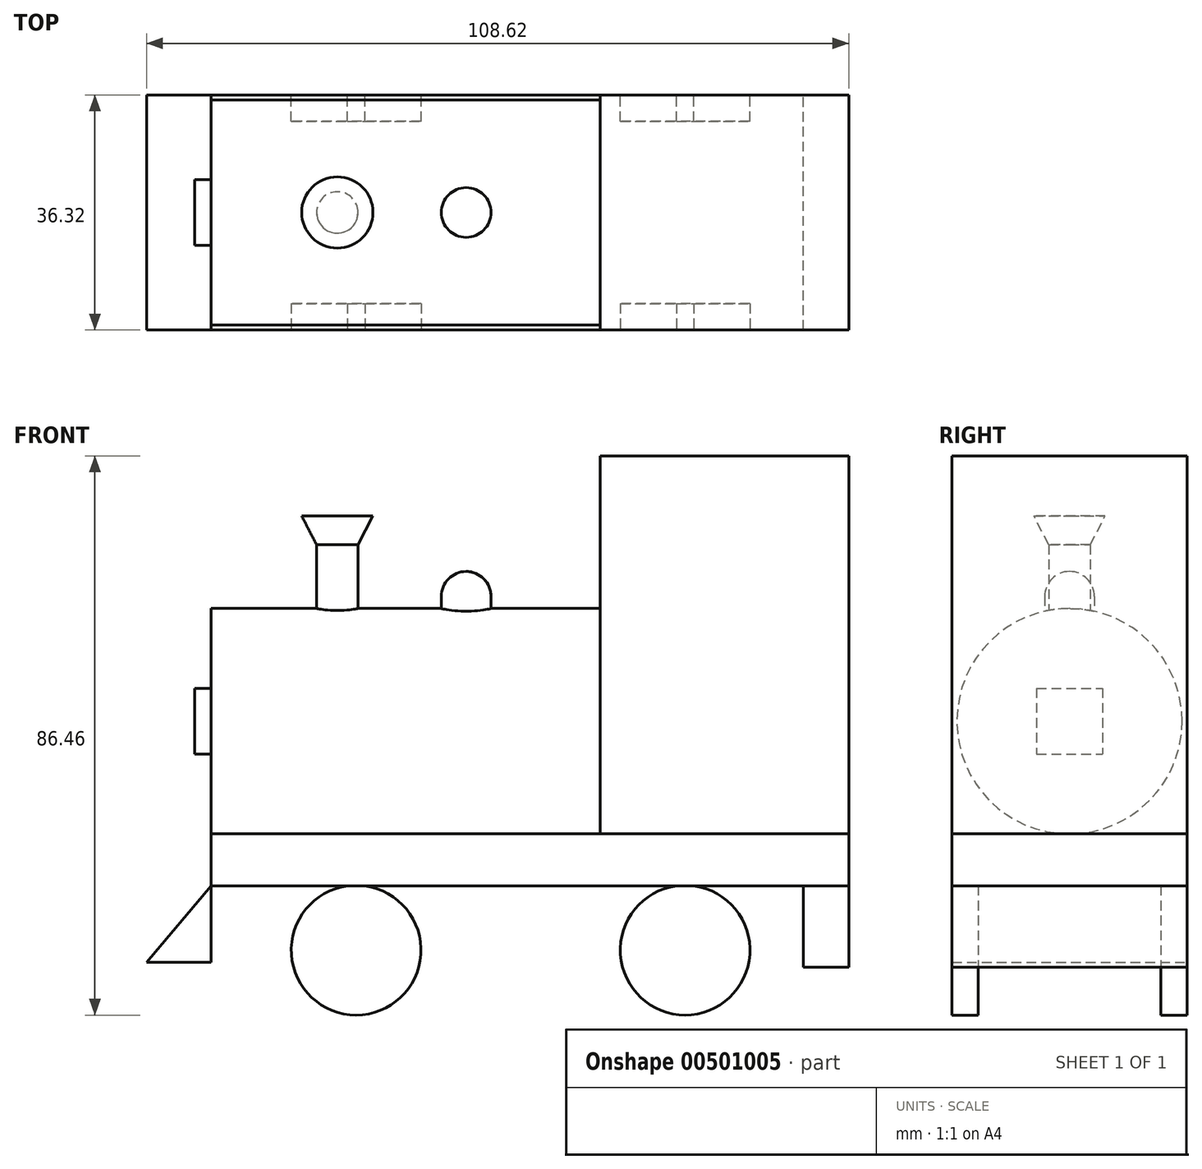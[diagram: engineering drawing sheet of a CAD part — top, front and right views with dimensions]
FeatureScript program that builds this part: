
annotation { "Feature Type Name" : "Feature", "Feature Type Description" : "" }
export const myFeature = defineFeature(function(context is Context, id is Id, definition is map)
    precondition{}
    {
        {
            var Q0;
            Q0=qCreatedBy(makeId("Front.planeOp"),FACE);
            var sketch = newSketch(context, id + "F0", { "sketchPlane" : qUnion([Q0])});
            skLineSegment(sketch, "E0.bottom", {"start": v(-47.1, -11.4) * mm, "end": v(51.53, -11.4) * mm});
            skLineSegment(sketch, "E0.top", {"start": v(-47.1, -19.43) * mm, "end": v(51.53, -19.43) * mm});
            skLineSegment(sketch, "E0.left", {"start": v(-47.1, -11.4) * mm, "end": v(-47.1, -19.43) * mm});
            skLineSegment(sketch, "E0.right", {"start": v(51.53, -11.4) * mm, "end": v(51.53, -19.43) * mm});
            skSolve(sketch);
        }
        {
            var Q0;
            Q0 = qSketchRegion(id + "F0", true);
            extrude(context, id + "F1", {"entities" : qUnion([Q0]), "oppositeDirection" : true, "depth" : 36.32 * mm, "symmetric" : true});
        }
        {
            var Q0;
            Q0=makeQuery(id+"F1.opExtrude","SWEPT_FACE",FACE,{"disambiguationData":[OSD([sQuery(id+"F0.wireOp",EDGE,"E0.left")])]});
            var sketch = newSketch(context, id + "F2", { "sketchPlane" : qUnion([Q0])});
            skCircle(sketch, "E1", {"center": v(0, 6.03) * mm, "radius": 17.42 * mm});
            skSolve(sketch);
        }
        {
            var Q0;
            Q0 = qSketchRegion(id + "F2", true);
            extrude(context, id + "F3", {"entities" : qUnion([Q0]), "operationType" : NewBodyOperationType.ADD, "oppositeDirection" : true, "depth" : 60.2 * mm});
        }
        {
            var Q0;
            Q0=makeQuery(id+"F3.opExtrude","CAP_FACE",FACE,{"disambiguationData":[OSD([sQuery(id+"F2.wireOp",EDGE,"E1")])],"isStart":false});
            var sketch = newSketch(context, id + "F4", { "sketchPlane" : qUnion([Q0])});
            skLineSegment(sketch, "E2.0", {"start": v(18.16, -11.4) * mm, "end": v(-18.16, -11.4) * mm});
            skLineSegment(sketch, "E3.top", {"start": v(18.16, 47.04) * mm, "end": v(-18.16, 47.04) * mm});
            skLineSegment(sketch, "E3.left", {"start": v(18.16, -11.4) * mm, "end": v(18.16, 47.04) * mm});
            skLineSegment(sketch, "E3.right", {"start": v(-18.16, -11.4) * mm, "end": v(-18.16, 47.04) * mm});
            skPoint(sketch, "E3.middle", {"position": v(0, 17.82) * mm});
            skPoint(sketch, "E3.middle.positionSnap0", {"position": v(0, -11.4) * mm});
            skPoint(sketch, "E3.centerSnap0", {"position": v(0, -11.4) * mm});
            skSolve(sketch);
        }
        {
            var Q0;
            Q0 = qSketchRegion(id + "F4", true);
            var Q1;
            Q1=makeQuery(id+"F1.opExtrude","SWEPT_FACE",FACE,{"disambiguationData":[OSD([sQuery(id+"F0.wireOp",EDGE,"E0.right")])]});
            extrude(context, id + "F5", {"entities" : qUnion([Q0]), "endBound" : BoundingType.UP_TO_SURFACE, "endBoundEntityFace" : qUnion([Q1]), "depth" : 17.78 * mm});
        }
        {
            var Q0;
            Q0=qCreatedBy(makeId("Front.planeOp"),FACE);
            var sketch = newSketch(context, id + "F6", { "sketchPlane" : qUnion([Q0])});
            skLineSegment(sketch, "E4", {"start": v(-27.6, 18.2) * mm, "end": v(-24.39, 18.2) * mm});
            skLineSegment(sketch, "E5", {"start": v(-24.39, 18.2) * mm, "end": v(-24.39, 33.31) * mm});
            skLineSegment(sketch, "E6", {"start": v(-24.39, 33.31) * mm, "end": v(-22.08, 37.76) * mm});
            skLineSegment(sketch, "E7", {"start": v(-27.6, 18.2) * mm, "end": v(-27.6, 48.43) * mm, "construction": true});
            skLineSegment(sketch, "E8", {"start": v(-22.08, 37.76) * mm, "end": v(-27.6, 37.76) * mm});
            skLineSegment(sketch, "E9", {"start": v(-27.6, 37.76) * mm, "end": v(-27.6, 18.2) * mm});
            skSolve(sketch);
        }
        {
            var Q0;
            Q0 = qSketchRegion(id + "F6", true);
            var Q1;
            Q1=sQuery(id+"F6.wireOp",EDGE,"E7");
            revolve(context, id + "F7", {"operationType" : NewBodyOperationType.ADD, "surfaceOperationType" : NewSurfaceOperationType.NEW, "entities" : qUnion([Q0]), "axis" : qUnion([Q1]), "revolveType" : RevolveType.FULL});
        }
        {
            var Q0;
            Q0=makeQuery(id+"F1.opExtrude","CAP_FACE",FACE,{"disambiguationData":[OSD([sQuery(id+"F0.wireOp",EDGE,"E0.bottom"),sQuery(id+"F0.wireOp",EDGE,"E0.top"),sQuery(id+"F0.wireOp",EDGE,"E0.left"),sQuery(id+"F0.wireOp",EDGE,"E0.right")])],"isStart":false});
            var sketch = newSketch(context, id + "F8", { "sketchPlane" : qUnion([Q0])});
            skCircle(sketch, "E10", {"center": v(24.68, -29.38) * mm, "radius": 10.04 * mm});
            skCircle(sketch, "E11", {"center": v(-26.22, -29.38) * mm, "radius": 10.04 * mm});
            skSolve(sketch);
        }
        {
            var Q0;
            Q0 = qSketchRegion(id + "F8", true);
            extrude(context, id + "F9", {"entities" : qUnion([Q0]), "operationType" : NewBodyOperationType.ADD, "oppositeDirection" : true, "depth" : 4.06 * mm});
        }
        {
            var Q0;
            Q0=makeQuery(id+"F1.opExtrude","SWEPT_BODY",BODY,{"disambiguationData":[OSD([sQuery(id+"F0.wireOp",EDGE,"E0.bottom"),sQuery(id+"F0.wireOp",EDGE,"E0.top"),sQuery(id+"F0.wireOp",EDGE,"E0.left"),sQuery(id+"F0.wireOp",EDGE,"E0.right")])]});
            var Q1;
            Q1=qCreatedBy(makeId("Front.planeOp"),FACE);
            mirror(context, id + "F10", {"entities" : qUnion([Q0]), "mirrorPlane" : qUnion([Q1])});
        }
        {
            var Q0;
            Q0=makeQuery(id+"F10.opPattern","COPY",FACE,{"derivedFrom":makeQuery(id+"F1.opExtrude","CAP_FACE",FACE,{"disambiguationData":[OSD([sQuery(id+"F0.wireOp",EDGE,"E0.bottom"),sQuery(id+"F0.wireOp",EDGE,"E0.top"),sQuery(id+"F0.wireOp",EDGE,"E0.left"),sQuery(id+"F0.wireOp",EDGE,"E0.right")])],"isStart":true}),"instanceName":"1"});
            var sketch = newSketch(context, id + "F11", { "sketchPlane" : qUnion([Q0])});
            skLineSegment(sketch, "E12", {"start": v(47.1, -19.43) * mm, "end": v(57.1, -31.23) * mm});
            skLineSegment(sketch, "E13", {"start": v(57.1, -31.23) * mm, "end": v(47.1, -31.23) * mm});
            skLineSegment(sketch, "E14", {"start": v(47.1, -31.23) * mm, "end": v(47.1, -19.43) * mm});
            skSolve(sketch);
        }
        {
            var Q0;
            Q0 = qSketchRegion(id + "F11", true);
            var Q1;
            Q1=makeQuery(id+"F10.opPattern","COPY",FACE,{"derivedFrom":makeQuery(id+"F9.boolean.opBoolean","MERGE",FACE,{"derivedFrom":[makeQuery(id+"F1.opExtrude","CAP_FACE",FACE,{"disambiguationData":[OSD([sQuery(id+"F0.wireOp",EDGE,"E0.bottom"),sQuery(id+"F0.wireOp",EDGE,"E0.top"),sQuery(id+"F0.wireOp",EDGE,"E0.left"),sQuery(id+"F0.wireOp",EDGE,"E0.right")])],"isStart":false}),makeQuery(id+"F9.opExtrude","CAP_FACE",FACE,{"disambiguationData":[OSD([sQuery(id+"F8.wireOp",EDGE,"E10")])],"isStart":true}),makeQuery(id+"F9.opExtrude","CAP_FACE",FACE,{"disambiguationData":[OSD([sQuery(id+"F8.wireOp",EDGE,"E11")])],"isStart":true})]}),"instanceName":"1"});
            extrude(context, id + "F12", {"entities" : qUnion([Q0]), "endBound" : BoundingType.UP_TO_SURFACE, "oppositeDirection" : true, "endBoundEntityFace" : qUnion([Q1]), "depth" : 25.4 * mm});
        }
        {
            var Q0;
            Q0=qCreatedBy(makeId("Front.planeOp"),FACE);
            var sketch = newSketch(context, id + "F13", { "sketchPlane" : qUnion([Q0])});
            skLineSegment(sketch, "E15", {"start": v(-7.66, 17.2) * mm, "end": v(-3.81, 17.2) * mm});
            skLineSegment(sketch, "E16", {"start": v(-3.81, 17.2) * mm, "end": v(-3.81, 25.33) * mm});
            skLineSegment(sketch, "E17", {"start": v(-7.66, 17.2) * mm, "end": v(-7.66, 42.78) * mm, "construction": true});
            skArc(sketch, "E18", {"start": v(-3.81, 25.33) * mm, "mid": v(-4.94, 28.05) * mm, "end": v(-7.66, 29.18) * mm});
            skLineSegment(sketch, "E19", {"start": v(-7.66, 17.2) * mm, "end": v(-7.66, 29.18) * mm});
            skSolve(sketch);
        }
        {
            var Q0;
            Q0 = qSketchRegion(id + "F13", true);
            var Q1;
            Q1=sQuery(id+"F13.wireOp",EDGE,"E17");
            revolve(context, id + "F14", {"operationType" : NewBodyOperationType.ADD, "surfaceOperationType" : NewSurfaceOperationType.NEW, "entities" : qUnion([Q0]), "axis" : qUnion([Q1]), "revolveType" : RevolveType.FULL});
        }
        {
            var Q0;
            Q0=makeQuery(id+"F9.boolean.opBoolean","MERGE",FACE,{"derivedFrom":[makeQuery(id+"F1.opExtrude","CAP_FACE",FACE,{"disambiguationData":[OSD([sQuery(id+"F0.wireOp",EDGE,"E0.bottom"),sQuery(id+"F0.wireOp",EDGE,"E0.top"),sQuery(id+"F0.wireOp",EDGE,"E0.left"),sQuery(id+"F0.wireOp",EDGE,"E0.right")])],"isStart":false}),makeQuery(id+"F9.opExtrude","CAP_FACE",FACE,{"disambiguationData":[OSD([sQuery(id+"F8.wireOp",EDGE,"E10")])],"isStart":true}),makeQuery(id+"F9.opExtrude","CAP_FACE",FACE,{"disambiguationData":[OSD([sQuery(id+"F8.wireOp",EDGE,"E11")])],"isStart":true})]});
            var sketch = newSketch(context, id + "F15", { "sketchPlane" : qUnion([Q0])});
            skLineSegment(sketch, "E20.bottom", {"start": v(-51.53, -19.43) * mm, "end": v(-44.5, -19.43) * mm});
            skLineSegment(sketch, "E20.top", {"start": v(-51.53, -32.03) * mm, "end": v(-44.5, -32.03) * mm});
            skLineSegment(sketch, "E20.left", {"start": v(-51.53, -19.43) * mm, "end": v(-51.53, -32.03) * mm});
            skLineSegment(sketch, "E20.right", {"start": v(-44.5, -19.43) * mm, "end": v(-44.5, -32.03) * mm});
            skSolve(sketch);
        }
        {
            var Q0;
            Q0 = qSketchRegion(id + "F15", true);
            var Q1;
            Q1=makeQuery(id+"F1.opExtrude","CAP_FACE",FACE,{"disambiguationData":[OSD([sQuery(id+"F0.wireOp",EDGE,"E0.bottom"),sQuery(id+"F0.wireOp",EDGE,"E0.top"),sQuery(id+"F0.wireOp",EDGE,"E0.left"),sQuery(id+"F0.wireOp",EDGE,"E0.right")])],"isStart":true});
            extrude(context, id + "F16", {"entities" : qUnion([Q0]), "endBound" : BoundingType.UP_TO_SURFACE, "oppositeDirection" : true, "endBoundEntityFace" : qUnion([Q1]), "depth" : 36.07 * mm});
        }
        {
            var Q0;
            Q0=makeQuery(id+"F3.opExtrude","CAP_FACE",FACE,{"disambiguationData":[OSD([sQuery(id+"F2.wireOp",EDGE,"E1")])],"isStart":true});
            var sketch = newSketch(context, id + "F17", { "sketchPlane" : qUnion([Q0])});
            skLineSegment(sketch, "E21.bottom", {"start": v(5.1, 11.12) * mm, "end": v(-5.1, 11.12) * mm});
            skLineSegment(sketch, "E21.top", {"start": v(5.1, 0.94) * mm, "end": v(-5.1, 0.94) * mm});
            skLineSegment(sketch, "E21.left", {"start": v(5.1, 11.12) * mm, "end": v(5.1, 0.94) * mm});
            skLineSegment(sketch, "E21.right", {"start": v(-5.1, 11.12) * mm, "end": v(-5.1, 0.94) * mm});
            skPoint(sketch, "E21.middle", {"position": v(0, 6.03) * mm});
            skSolve(sketch);
        }
        {
            var Q0;
            Q0 = qSketchRegion(id + "F17", true);
            extrude(context, id + "F18", {"entities" : qUnion([Q0]), "operationType" : NewBodyOperationType.ADD, "depth" : 2.54 * mm});
        }
    });
